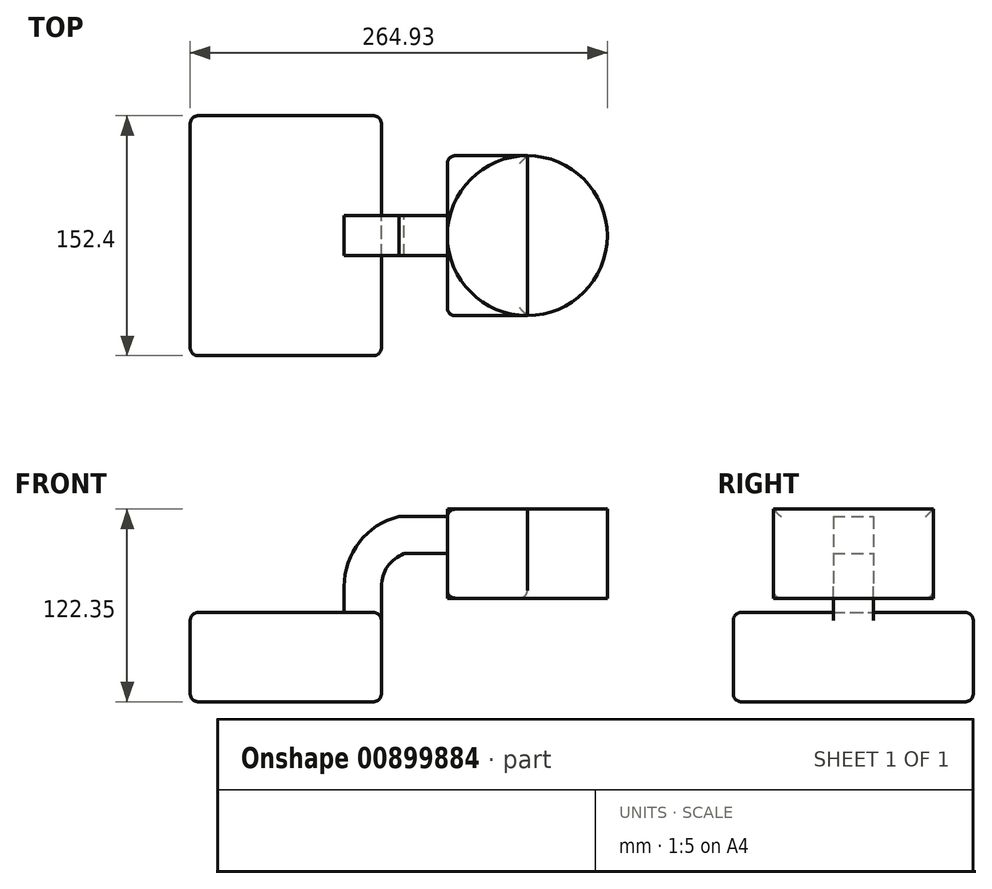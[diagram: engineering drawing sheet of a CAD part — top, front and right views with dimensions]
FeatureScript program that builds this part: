
annotation { "Feature Type Name" : "Feature", "Feature Type Description" : "" }
export const myFeature = defineFeature(function(context is Context, id is Id, definition is map)
    precondition{}
    {
        {
            var Q0;
            Q0=qCreatedBy(makeId("Front.planeOp"),FACE);
            var sketch = newSketch(context, id + "F0", { "sketchPlane" : qUnion([Q0])});
            skLineSegment(sketch, "E0.bottom", {"start": v(60.7, -28.35) * mm, "end": v(-60.7, -28.35) * mm});
            skLineSegment(sketch, "E0.top", {"start": v(60.7, 28.35) * mm, "end": v(-60.7, 28.35) * mm});
            skLineSegment(sketch, "E0.left", {"start": v(60.7, -28.35) * mm, "end": v(60.7, 28.35) * mm});
            skLineSegment(sketch, "E0.right", {"start": v(-60.7, -28.35) * mm, "end": v(-60.7, 28.35) * mm});
            skPoint(sketch, "E0.middle", {"position": v(0, 0) * mm});
            skLineSegment(sketch, "E1.bottom", {"start": v(102.62, 94) * mm, "end": v(153.42, 94) * mm});
            skLineSegment(sketch, "E1.top", {"start": v(102.62, 37.44) * mm, "end": v(153.42, 37.44) * mm});
            skLineSegment(sketch, "E1.left", {"start": v(102.62, 94) * mm, "end": v(102.62, 37.44) * mm});
            skLineSegment(sketch, "E1.right", {"start": v(153.42, 94) * mm, "end": v(153.42, 37.44) * mm});
            skLineSegment(sketch, "E2", {"start": v(60.7, 28.35) * mm, "end": v(60.7, 44.9) * mm});
            skArc(sketch, "E3", {"start": v(60.7, 44.9) * mm, "mid": v(64.7, 57.59) * mm, "end": v(75.23, 65.72) * mm});
            skPoint(sketch, "E3.endSnap0", {"position": v(102.62, 65.72) * mm});
            skLineSegment(sketch, "E4", {"start": v(75.23, 65.72) * mm, "end": v(102.62, 65.72) * mm});
            skLineSegment(sketch, "E5.0", {"start": v(71.8, 89.34) * mm, "end": v(103.22, 89.34) * mm});
            skArc(sketch, "E5.1", {"start": v(37.09, 44.9) * mm, "mid": v(46.8, 73.1) * mm, "end": v(71.8, 89.34) * mm});
            skLineSegment(sketch, "E5.2", {"start": v(37.09, 28.35) * mm, "end": v(37.09, 44.9) * mm});
            skFitSpline(sketch, "E6", {"points": [v(-60.7, 28.35) * mm, v(71.8, 89.34) * mm], "startDerivative": vector(80.43, 195.23) * mm, "endDerivative": vector(146.93, 3.28) * mm});
            skSolve(sketch);
        }
        {
            var Q0;
            Q0=makeQuery(id+"F0.imprint","IMPRINT",FACE,{"disambiguationData":[TD([[makeQuery(id+"F0.imprint","IMPRINT",EDGE,{"derivedFrom":sQuery(id+"F0.wireOp",EDGE,"E0.bottom")}),-1.0]])]});
            extrude(context, id + "F1", {"entities" : qUnion([Q0]), "endBound" : BoundingType.SYMMETRIC, "depth" : 152.4 * mm, "offsetDistance" : 25.4 * mm});
        }
        {
            var Q0;
            Q0=makeQuery(id+"F0.imprint","IMPRINT",FACE,{"disambiguationData":[TD([[makeQuery(id+"F0.imprint","IMPRINT",EDGE,{"derivedFrom":sQuery(id+"F0.wireOp",EDGE,"E5.1")}),1.0]])]});
            var Q1;
            {var subQ0=sQuery(id+"F0.wireOp",EDGE,"E2");Q1=makeQuery(id+"F0.imprint","IMPRINT",FACE,{"disambiguationData":[TD([[makeQuery(id+"F0.imprint","IMPRINT",EDGE,{"derivedFrom":subQ0}),1.0]])]});}
            extrude(context, id + "F2", {"entities" : qUnion([Q0, Q1]), "operationType" : NewBodyOperationType.ADD, "endBound" : BoundingType.SYMMETRIC, "depth" : 25.4 * mm, "offsetDistance" : 25.4 * mm});
        }
        {
            var Q0;
            {var subQ3=sQuery(id+"F0.wireOp",EDGE,"E1.bottom");Q0=makeQuery(id+"F0.imprint","IMPRINT",FACE,{"disambiguationData":[TD([[makeQuery(id+"F0.imprint","IMPRINT",EDGE,{"derivedFrom":subQ3}),-1.0]])]});}
            extrude(context, id + "F3", {"entities" : qUnion([Q0]), "operationType" : NewBodyOperationType.ADD, "endBound" : BoundingType.SYMMETRIC, "depth" : 101.6 * mm, "offsetDistance" : 25.4 * mm});
        }
        {
            var Q0;
            Q0=makeQuery(id+"F1.opExtrude","CAP_EDGE",EDGE,{"disambiguationData":[OSD([sQuery(id+"F0.wireOp",EDGE,"E0.top")])],"isStart":true});
            var Q1;
            Q1=makeQuery(id+"F1.opExtrude","CAP_EDGE",EDGE,{"disambiguationData":[OSD([sQuery(id+"F0.wireOp",EDGE,"E0.bottom")])],"isStart":true});
            var Q2;
            Q2=makeQuery(id+"F1.opExtrude","CAP_EDGE",EDGE,{"disambiguationData":[OSD([sQuery(id+"F0.wireOp",EDGE,"E0.right")])],"isStart":true});
            var Q3;
            Q3=makeQuery(id+"F1.opExtrude","CAP_EDGE",EDGE,{"disambiguationData":[OSD([sQuery(id+"F0.wireOp",EDGE,"E0.left")])],"isStart":true});
            var Q4;
            {var subQ0=sQuery(id+"F0.wireOp",EDGE,"E6");var subQ1=sQuery(id+"F0.wireOp",EDGE,"E0.top");var subQ2=sQuery(id+"F0.wireOp",EDGE,"E0.right");Q4=makeQuery(id+"F2.boolean.opBoolean","SPLIT",EDGE,{"disambiguationData":[TD([makeQuery(id+"F1.opExtrude","CAP_FACE",FACE,{"disambiguationData":[OSD([sQuery(id+"F0.wireOp",EDGE,"E0.bottom"),subQ1,sQuery(id+"F0.wireOp",EDGE,"E0.left"),subQ2])],"isStart":true})])],"derivedFrom":makeQuery(id+"F1.opExtrude","SWEPT_EDGE",EDGE,{"disambiguationData":[OSD([subQ1,subQ2,subQ0])]})});}
            var Q5;
            {var subQ0=sQuery(id+"F0.wireOp",EDGE,"E2");var subQ1=sQuery(id+"F0.wireOp",EDGE,"E0.top");var subQ2=sQuery(id+"F0.wireOp",EDGE,"E0.left");Q5=makeQuery(id+"F2.boolean.opBoolean","SPLIT",EDGE,{"disambiguationData":[TD([makeQuery(id+"F1.opExtrude","CAP_FACE",FACE,{"disambiguationData":[OSD([sQuery(id+"F0.wireOp",EDGE,"E0.bottom"),subQ1,subQ2,sQuery(id+"F0.wireOp",EDGE,"E0.right")])],"isStart":true})])],"derivedFrom":makeQuery(id+"F1.opExtrude","SWEPT_EDGE",EDGE,{"disambiguationData":[OSD([subQ1,subQ2,subQ0])]})});}
            var Q6;
            {var subQ0=sQuery(id+"F0.wireOp",EDGE,"E0.right");var subQ1=sQuery(id+"F0.wireOp",EDGE,"E6");var subQ2=sQuery(id+"F0.wireOp",EDGE,"E0.top");Q6=makeQuery(id+"F2.boolean.opBoolean","SPLIT",EDGE,{"disambiguationData":[TD([makeQuery(id+"F1.opExtrude","CAP_FACE",FACE,{"disambiguationData":[OSD([sQuery(id+"F0.wireOp",EDGE,"E0.bottom"),subQ2,sQuery(id+"F0.wireOp",EDGE,"E0.left"),subQ0])],"isStart":false})])],"derivedFrom":makeQuery(id+"F1.opExtrude","SWEPT_EDGE",EDGE,{"disambiguationData":[OSD([subQ2,subQ0,subQ1])]})});}
            var Q7;
            {var subQ0=sQuery(id+"F0.wireOp",EDGE,"E0.left");var subQ1=sQuery(id+"F0.wireOp",EDGE,"E2");var subQ2=sQuery(id+"F0.wireOp",EDGE,"E0.top");Q7=makeQuery(id+"F2.boolean.opBoolean","SPLIT",EDGE,{"disambiguationData":[TD([makeQuery(id+"F1.opExtrude","CAP_FACE",FACE,{"disambiguationData":[OSD([sQuery(id+"F0.wireOp",EDGE,"E0.bottom"),subQ2,subQ0,sQuery(id+"F0.wireOp",EDGE,"E0.right")])],"isStart":false})])],"derivedFrom":makeQuery(id+"F1.opExtrude","SWEPT_EDGE",EDGE,{"disambiguationData":[OSD([subQ2,subQ0,subQ1])]})});}
            var Q8;
            Q8=makeQuery(id+"F1.opExtrude","CAP_EDGE",EDGE,{"disambiguationData":[OSD([sQuery(id+"F0.wireOp",EDGE,"E0.top")])],"isStart":false});
            var Q9;
            Q9=makeQuery(id+"F1.opExtrude","CAP_EDGE",EDGE,{"disambiguationData":[OSD([sQuery(id+"F0.wireOp",EDGE,"E0.bottom")])],"isStart":false});
            var Q10;
            Q10=makeQuery(id+"F1.opExtrude","CAP_EDGE",EDGE,{"disambiguationData":[OSD([sQuery(id+"F0.wireOp",EDGE,"E0.left")])],"isStart":false});
            var Q11;
            Q11=makeQuery(id+"F1.opExtrude","CAP_EDGE",EDGE,{"disambiguationData":[OSD([sQuery(id+"F0.wireOp",EDGE,"E0.right")])],"isStart":false});
            var Q12;
            Q12=makeQuery(id+"F1.opExtrude","SWEPT_EDGE",EDGE,{"disambiguationData":[OSD([sQuery(id+"F0.wireOp",EDGE,"E0.bottom"),sQuery(id+"F0.wireOp",EDGE,"E0.right")])]});
            var Q13;
            Q13=makeQuery(id+"F1.opExtrude","SWEPT_EDGE",EDGE,{"disambiguationData":[OSD([sQuery(id+"F0.wireOp",EDGE,"E0.bottom"),sQuery(id+"F0.wireOp",EDGE,"E0.left")])]});
            var Q14;
            Q14=makeQuery(id+"F3.opExtrude","SWEPT_EDGE",EDGE,{"disambiguationData":[OSD([sQuery(id+"F0.wireOp",EDGE,"E1.top"),sQuery(id+"F0.wireOp",EDGE,"E1.right")])]});
            var Q15;
            Q15=makeQuery(id+"F3.opExtrude","CAP_EDGE",EDGE,{"disambiguationData":[OSD([sQuery(id+"F0.wireOp",EDGE,"E1.left")])],"isStart":false});
            var Q16;
            Q16=makeQuery(id+"F3.opExtrude","CAP_EDGE",EDGE,{"disambiguationData":[OSD([sQuery(id+"F0.wireOp",EDGE,"E1.top")])],"isStart":false});
            var Q17;
            Q17=makeQuery(id+"F3.opExtrude","SWEPT_EDGE",EDGE,{"disambiguationData":[OSD([sQuery(id+"F0.wireOp",EDGE,"E1.bottom"),sQuery(id+"F0.wireOp",EDGE,"E1.left")])]});
            var Q18;
            Q18=makeQuery(id+"F3.opExtrude","SWEPT_EDGE",EDGE,{"disambiguationData":[OSD([sQuery(id+"F0.wireOp",EDGE,"E1.top"),sQuery(id+"F0.wireOp",EDGE,"E1.left")])]});
            var Q19;
            Q19=makeQuery(id+"F3.opExtrude","CAP_EDGE",EDGE,{"disambiguationData":[OSD([sQuery(id+"F0.wireOp",EDGE,"E1.left")])],"isStart":true});
            var Q20;
            Q20=makeQuery(id+"F3.opExtrude","CAP_EDGE",EDGE,{"disambiguationData":[OSD([sQuery(id+"F0.wireOp",EDGE,"E1.top")])],"isStart":true});
            fillet(context, id + "F4", {"entities" : qUnion([Q0, Q1, Q2, Q3, Q4, Q5, Q6, Q7, Q8, Q9, Q10, Q11, Q12, Q13, Q14, Q15, Q16, Q17, Q18, Q19, Q20]), "radius" : 5.08 * mm, "tangentPropagation" : true, "allowEdgeOverflow" : false});
        }
        {
            var Q0;
            {var subQ3=sQuery(id+"F0.wireOp",EDGE,"E1.bottom");Q0=makeQuery(id+"F0.imprint","IMPRINT",FACE,{"disambiguationData":[TD([[makeQuery(id+"F0.imprint","IMPRINT",EDGE,{"derivedFrom":subQ3}),-1.0]])]});}
            var Q1;
            Q1=sQuery(id+"F0.wireOp",EDGE,"E1.right");
            revolve(context, id + "F5", {"surfaceOperationType" : NewSurfaceOperationType.NEW, "entities" : qUnion([Q0]), "axis" : qUnion([Q1]), "revolveType" : RevolveType.FULL});
        }
    });
